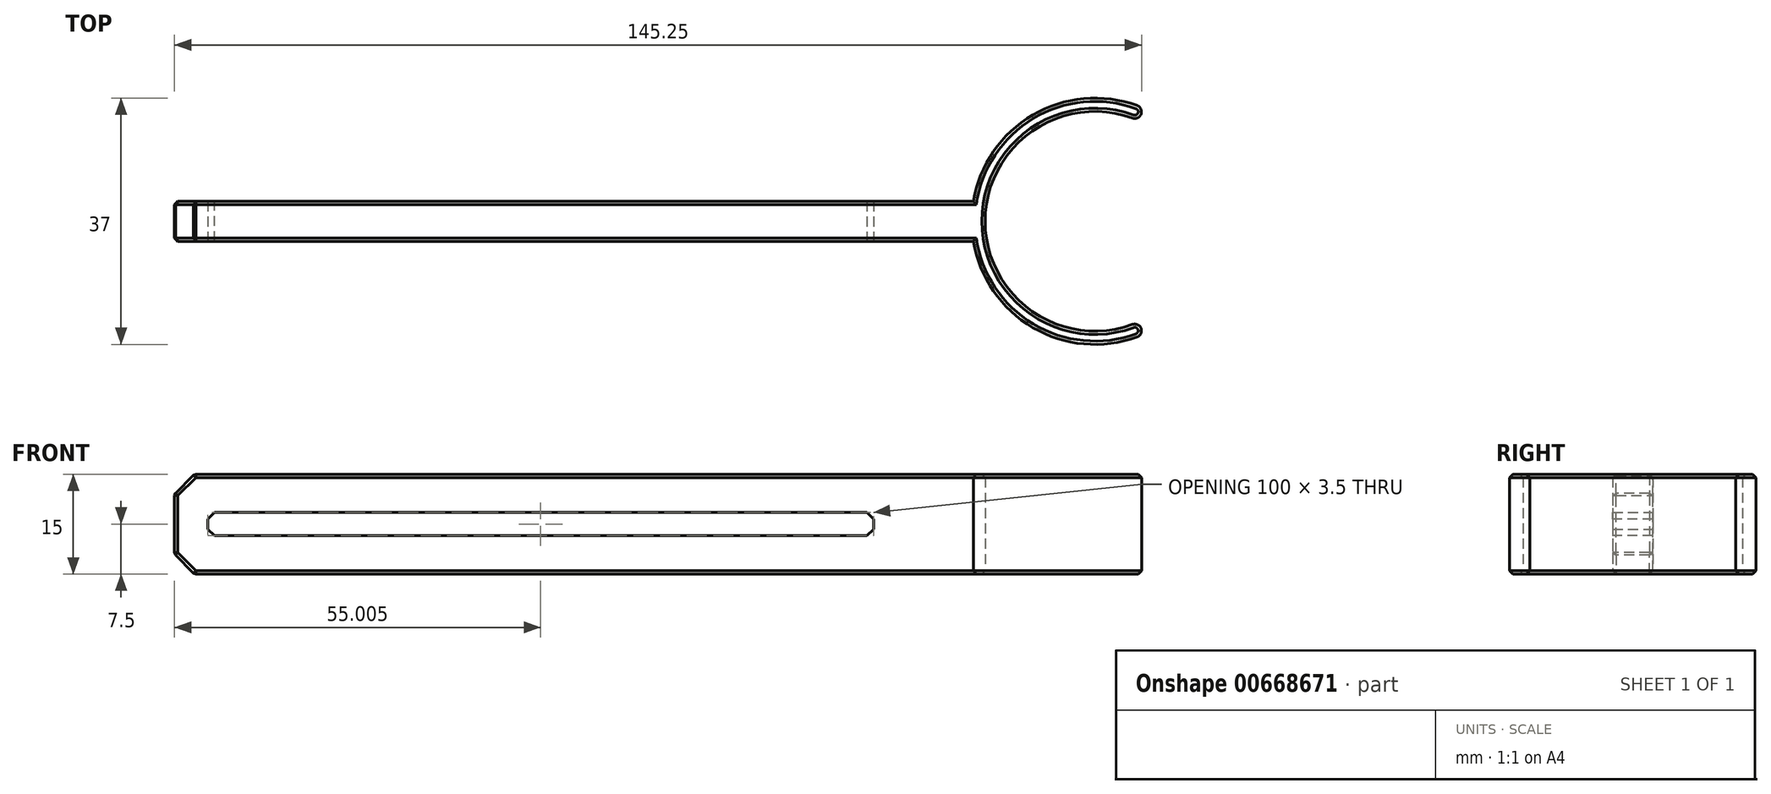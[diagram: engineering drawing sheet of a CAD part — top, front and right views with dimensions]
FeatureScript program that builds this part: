
annotation { "Feature Type Name" : "Feature", "Feature Type Description" : "" }
export const myFeature = defineFeature(function(context is Context, id is Id, definition is map)
    precondition{}
    {
        {
            var Q0;
            Q0=qCreatedBy(makeId("Top.planeOp"),FACE);
            var sketch = newSketch(context, id + "F0", { "sketchPlane" : qUnion([Q0])});
            skArc(sketch, "E0", {"start": v(6.33, 17.38) * mm, "mid": v(-9.34, 15.97) * mm, "end": v(-18.26, 3) * mm});
            skLineSegment(sketch, "E1", {"start": v(6.33, -17.38) * mm, "end": v(0, 0) * mm, "construction": true});
            skLineSegment(sketch, "E2", {"start": v(6.33, 17.38) * mm, "end": v(0, 0) * mm, "construction": true});
            skArc(sketch, "E3", {"start": v(5.64, 15.5) * mm, "mid": v(-16.5, 0) * mm, "end": v(5.64, -15.5) * mm});
            skLineSegment(sketch, "E4", {"start": v(-18.26, 3) * mm, "end": v(-138.26, 3) * mm});
            skLineSegment(sketch, "E5", {"start": v(-138.26, 3) * mm, "end": v(-138.26, -3) * mm});
            skLineSegment(sketch, "E6", {"start": v(-138.26, -3) * mm, "end": v(-18.26, -3) * mm});
            skArc(sketch, "E7.trimOffspring", {"start": v(-18.26, -3) * mm, "mid": v(-9.34, -15.97) * mm, "end": v(6.33, -17.38) * mm});
            skArc(sketch, "E8", {"start": v(6.33, 17.38) * mm, "mid": v(6.93, 16.1) * mm, "end": v(5.64, 15.5) * mm});
            skArc(sketch, "E9", {"start": v(5.64, -15.5) * mm, "mid": v(6.93, -16.1) * mm, "end": v(6.33, -17.38) * mm});
            skSolve(sketch);
        }
        {
            var Q0;
            Q0 = qSketchRegion(id + "F0", true);
            extrude(context, id + "F1", {"entities" : qUnion([Q0]), "depth" : 15 * mm, "offsetDistance" : 25 * mm, "symmetric" : true});
        }
        {
            var Q0;
            Q0=makeQuery(id+"F1.opExtrude","SWEPT_FACE",FACE,{"disambiguationData":[OSD([sQuery(id+"F0.wireOp",EDGE,"E6")])]});
            var sketch = newSketch(context, id + "F2", { "sketchPlane" : qUnion([Q0])});
            skLineSegment(sketch, "E10.bottom", {"start": v(-133.26, 1.75) * mm, "end": v(-33.26, 1.75) * mm});
            skLineSegment(sketch, "E10.top", {"start": v(-133.26, -1.75) * mm, "end": v(-33.26, -1.75) * mm});
            skLineSegment(sketch, "E10.left", {"start": v(-133.26, 1.75) * mm, "end": v(-133.26, -1.75) * mm});
            skLineSegment(sketch, "E10.right", {"start": v(-33.26, 1.75) * mm, "end": v(-33.26, -1.75) * mm});
            skSolve(sketch);
        }
        {
            var Q0;
            Q0 = qSketchRegion(id + "F2", true);
            extrude(context, id + "F3", {"entities" : qUnion([Q0]), "operationType" : NewBodyOperationType.REMOVE, "endBound" : BoundingType.THROUGH_ALL, "oppositeDirection" : true, "depth" : 25 * mm, "offsetDistance" : 25 * mm});
        }
        {
            var Q0;
            Q0=makeQuery(id+"F1.opExtrude","CAP_EDGE",EDGE,{"disambiguationData":[OSD([sQuery(id+"F0.wireOp",EDGE,"E5")])],"isStart":false});
            var Q1;
            Q1=makeQuery(id+"F1.opExtrude","CAP_EDGE",EDGE,{"disambiguationData":[OSD([sQuery(id+"F0.wireOp",EDGE,"E5")])],"isStart":true});
            chamfer(context, id + "F4", {"entities" : qUnion([Q0, Q1]), "width" : 3 * mm, "tangentPropagation" : true});
        }
        {
            var Q0;
            Q0=makeQuery(id+"F3.boolean.opBoolean","COPY",EDGE,{"derivedFrom":makeQuery(id+"F3.opExtrude","SWEPT_EDGE",EDGE,{"disambiguationData":[OSD([sQuery(id+"F2.wireOp",EDGE,"E10.bottom"),sQuery(id+"F2.wireOp",EDGE,"E10.right")])]})});
            var Q1;
            Q1=makeQuery(id+"F3.boolean.opBoolean","COPY",EDGE,{"derivedFrom":makeQuery(id+"F3.opExtrude","SWEPT_EDGE",EDGE,{"disambiguationData":[OSD([sQuery(id+"F2.wireOp",EDGE,"E10.top"),sQuery(id+"F2.wireOp",EDGE,"E10.right")])]})});
            var Q2;
            Q2=makeQuery(id+"F3.boolean.opBoolean","COPY",EDGE,{"derivedFrom":makeQuery(id+"F3.opExtrude","SWEPT_EDGE",EDGE,{"disambiguationData":[OSD([sQuery(id+"F2.wireOp",EDGE,"E10.bottom"),sQuery(id+"F2.wireOp",EDGE,"E10.left")])]})});
            var Q3;
            Q3=makeQuery(id+"F3.boolean.opBoolean","COPY",EDGE,{"derivedFrom":makeQuery(id+"F3.opExtrude","SWEPT_EDGE",EDGE,{"disambiguationData":[OSD([sQuery(id+"F2.wireOp",EDGE,"E10.top"),sQuery(id+"F2.wireOp",EDGE,"E10.left")])]})});
            chamfer(context, id + "F5", {"entities" : qUnion([Q0, Q1, Q2, Q3]), "width" : 1 * mm, "tangentPropagation" : true});
        }
        {
            var Q0;
            Q0=makeQuery(id+"F1.opExtrude","CAP_FACE",FACE,{"disambiguationData":[OSD([sQuery(id+"F0.wireOp",EDGE,"E0"),sQuery(id+"F0.wireOp",EDGE,"E3"),sQuery(id+"F0.wireOp",EDGE,"E4"),sQuery(id+"F0.wireOp",EDGE,"E5"),sQuery(id+"F0.wireOp",EDGE,"E6"),sQuery(id+"F0.wireOp",EDGE,"E7.trimOffspring"),sQuery(id+"F0.wireOp",EDGE,"E8"),sQuery(id+"F0.wireOp",EDGE,"E9")])],"isStart":false});
            var Q1;
            Q1=makeQuery(id+"F1.opExtrude","CAP_FACE",FACE,{"disambiguationData":[OSD([sQuery(id+"F0.wireOp",EDGE,"E0"),sQuery(id+"F0.wireOp",EDGE,"E3"),sQuery(id+"F0.wireOp",EDGE,"E4"),sQuery(id+"F0.wireOp",EDGE,"E5"),sQuery(id+"F0.wireOp",EDGE,"E6"),sQuery(id+"F0.wireOp",EDGE,"E7.trimOffspring"),sQuery(id+"F0.wireOp",EDGE,"E8"),sQuery(id+"F0.wireOp",EDGE,"E9")])],"isStart":true});
            var Q2;
            {var subQ0=sQuery(id+"F0.wireOp",EDGE,"E5");Q2=makeQuery(id+"F4.opChamfer","BLEND_FACE",FACE,{"disambiguationData":[OSD([subQ0]),TDD([makeQuery(id+"F1.opExtrude","CAP_EDGE",EDGE,{"disambiguationData":[OSD([subQ0])],"isStart":true})])]});}
            var Q3;
            {var subQ0=sQuery(id+"F0.wireOp",EDGE,"E5");Q3=makeQuery(id+"F4.opChamfer","BLEND_FACE",FACE,{"disambiguationData":[OSD([subQ0]),TDD([makeQuery(id+"F1.opExtrude","CAP_EDGE",EDGE,{"disambiguationData":[OSD([subQ0])],"isStart":false})])]});}
            var Q4;
            Q4=makeQuery(id+"F1.opExtrude","SWEPT_FACE",FACE,{"disambiguationData":[OSD([sQuery(id+"F0.wireOp",EDGE,"E5")])]});
            chamfer(context, id + "F6", {"entities" : qUnion([Q0, Q1, Q2, Q3, Q4]), "width" : .5 * mm, "tangentPropagation" : true});
        }
    });
